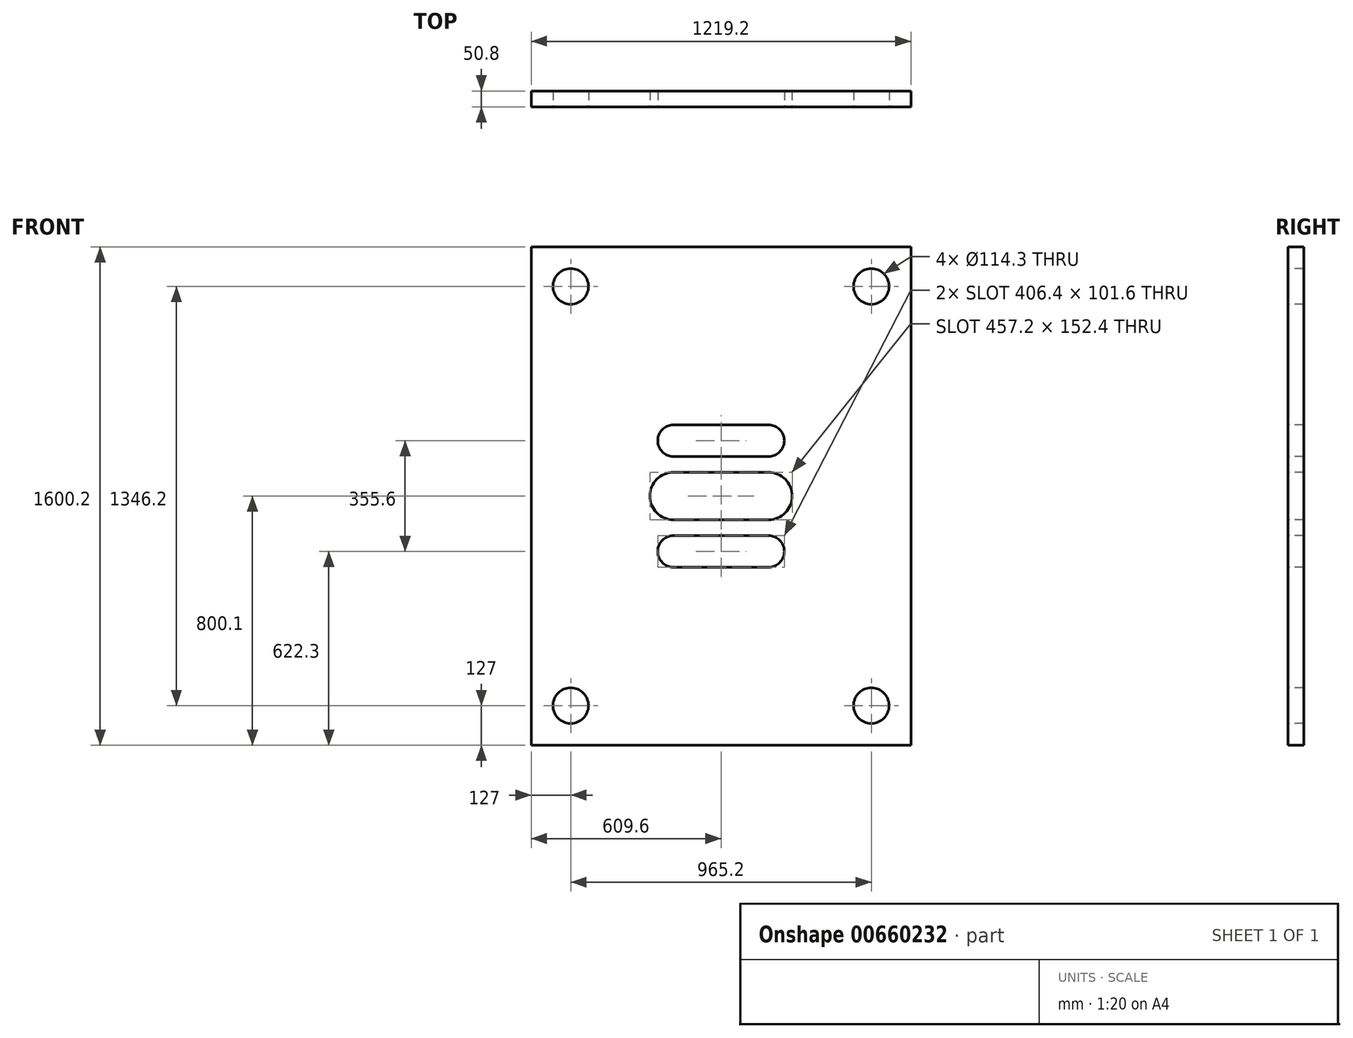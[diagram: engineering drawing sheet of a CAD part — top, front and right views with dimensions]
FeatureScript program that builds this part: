
annotation { "Feature Type Name" : "Feature", "Feature Type Description" : "" }
export const myFeature = defineFeature(function(context is Context, id is Id, definition is map)
    precondition{}
    {
        {
            var Q0;
            Q0=qCreatedBy(makeId("Front.planeOp"),FACE);
            var sketch = newSketch(context, id + "F0", { "sketchPlane" : qUnion([Q0])});
            skLineSegment(sketch, "E0.bottom", {"start": v(-609.6, -800.1) * mm, "end": v(609.6, -800.1) * mm});
            skLineSegment(sketch, "E0.top", {"start": v(-609.6, 800.1) * mm, "end": v(609.6, 800.1) * mm});
            skLineSegment(sketch, "E0.left", {"start": v(-609.6, -800.1) * mm, "end": v(-609.6, 800.1) * mm});
            skLineSegment(sketch, "E0.right", {"start": v(609.6, -800.1) * mm, "end": v(609.6, 800.1) * mm});
            skPoint(sketch, "E0.middle", {"position": v(0, 0) * mm});
            skSolve(sketch);
        }
        {
            var Q0;
            Q0=makeQuery(id+"F0.imprint","IMPRINT",FACE,{"disambiguationData":[TD([[makeQuery(id+"F0.imprint","IMPRINT",EDGE,{"derivedFrom":sQuery(id+"F0.wireOp",EDGE,"E0.bottom")}),1.0]])]});
            var sketch = newSketch(context, id + "F1", { "sketchPlane" : qUnion([Q0])});
            skLineSegment(sketch, "E1", {"start": v(0, 743.78) * mm, "end": v(0, -755.56) * mm, "construction": true});
            skSolve(sketch);
        }
        {
            var Q0;
            Q0=makeQuery(id+"F1.imprint","IMPRINT",FACE,{"disambiguationData":[TD([[makeQuery(id+"F1.imprint","IMPRINT",EDGE,{"derivedFrom":makeQuery(id+"F0.imprint","IMPRINT",EDGE,{"derivedFrom":sQuery(id+"F0.wireOp",EDGE,"E0.bottom")})}),1.0]])]});
            extrude(context, id + "F2", {"entities" : qUnion([Q0]), "depth" : 50.8 * mm, "offsetDistance" : 25.4 * mm});
        }
        {
            var Q0;
            Q0=makeQuery(id+"F2.opExtrude","CAP_FACE",FACE,{"disambiguationData":[OSD([sQuery(id+"F0.wireOp",EDGE,"E0.bottom"),sQuery(id+"F0.wireOp",EDGE,"E0.top"),sQuery(id+"F0.wireOp",EDGE,"E0.left"),sQuery(id+"F0.wireOp",EDGE,"E0.right")])],"isStart":false});
            var sketch = newSketch(context, id + "F3", { "sketchPlane" : qUnion([Q0])});
            skCircle(sketch, "E2", {"center": v(-482.6, 673.1) * mm, "radius": 57.15 * mm});
            skLineSegment(sketch, "E3", {"start": v(-506.12, 0) * mm, "end": v(142.94, 0) * mm, "construction": true});
            skLineSegment(sketch, "E4", {"start": v(0, 664.01) * mm, "end": v(0, -622.38) * mm, "construction": true});
            skCircle(sketch, "E5.MirrorC", {"center": v(482.6, 673.1) * mm, "radius": 57.15 * mm});
            skCircle(sketch, "E6.MirrorC", {"center": v(-482.6, -673.1) * mm, "radius": 57.15 * mm});
            skCircle(sketch, "E7.MirrorC", {"center": v(482.6, -673.1) * mm, "radius": 57.15 * mm});
            skSolve(sketch);
        }
        {
            var Q0;
            Q0 = qSketchRegion(id + "F3", true);
            extrude(context, id + "F4", {"entities" : qUnion([Q0]), "operationType" : NewBodyOperationType.REMOVE, "oppositeDirection" : true, "depth" : 76.2 * mm, "offsetDistance" : 25.4 * mm});
        }
        {
            var Q0;
            Q0=makeQuery(id+"F2.opExtrude","CAP_FACE",FACE,{"disambiguationData":[OSD([sQuery(id+"F0.wireOp",EDGE,"E0.bottom"),sQuery(id+"F0.wireOp",EDGE,"E0.top"),sQuery(id+"F0.wireOp",EDGE,"E0.left"),sQuery(id+"F0.wireOp",EDGE,"E0.right")])],"isStart":false});
            var sketch = newSketch(context, id + "F5", { "sketchPlane" : qUnion([Q0])});
            skLineSegment(sketch, "E8.bottom", {"start": v(-152.4, 127) * mm, "end": v(152.4, 127) * mm});
            skLineSegment(sketch, "E8.top", {"start": v(-152.4, 228.6) * mm, "end": v(152.4, 228.6) * mm});
            skLineSegment(sketch, "E8.left", {"start": v(-152.4, 127) * mm, "end": v(-152.4, 228.6) * mm});
            skLineSegment(sketch, "E8.right", {"start": v(152.4, 127) * mm, "end": v(152.4, 228.6) * mm});
            skPoint(sketch, "E8.middle", {"position": v(0, 177.8) * mm});
            skArc(sketch, "E9", {"start": v(152.4, 127) * mm, "mid": v(203.2, 177.8) * mm, "end": v(152.4, 228.6) * mm});
            skArc(sketch, "E10", {"start": v(-152.4, 228.6) * mm, "mid": v(-203.2, 177.8) * mm, "end": v(-152.4, 127) * mm});
            skLineSegment(sketch, "E11", {"start": v(-215.96, 0) * mm, "end": v(248.62, 0) * mm, "construction": true});
            skLineSegment(sketch, "E12.MirrorCS", {"start": v(-152.4, -127) * mm, "end": v(152.4, -127) * mm});
            skLineSegment(sketch, "E13.MirrorCS", {"start": v(-152.4, -228.6) * mm, "end": v(152.4, -228.6) * mm});
            skArc(sketch, "E14.MirrorCS", {"start": v(152.4, -127) * mm, "mid": v(203.2, -177.8) * mm, "end": v(152.4, -228.6) * mm});
            skArc(sketch, "E15.MirrorCS", {"start": v(-152.4, -228.6) * mm, "mid": v(-203.2, -177.8) * mm, "end": v(-152.4, -127) * mm});
            skLineSegment(sketch, "E16.bottom", {"start": v(-152.4, -76.2) * mm, "end": v(152.4, -76.2) * mm});
            skLineSegment(sketch, "E16.top", {"start": v(-152.4, 76.2) * mm, "end": v(152.4, 76.2) * mm});
            skLineSegment(sketch, "E16.left", {"start": v(-152.4, -76.2) * mm, "end": v(-152.4, 76.2) * mm});
            skLineSegment(sketch, "E16.right", {"start": v(152.4, -76.2) * mm, "end": v(152.4, 76.2) * mm});
            skPoint(sketch, "E16.middle", {"position": v(0, 0) * mm});
            skArc(sketch, "E17", {"start": v(152.4, -76.2) * mm, "mid": v(228.6, 0) * mm, "end": v(152.4, 76.2) * mm});
            skLineSegment(sketch, "E18", {"start": v(0, 0) * mm, "end": v(0, -76.2) * mm, "construction": true});
            skArc(sketch, "E19.MirrorCS", {"start": v(-152.4, -76.2) * mm, "mid": v(-228.6, 0) * mm, "end": v(-152.4, 76.2) * mm});
            skSolve(sketch);
        }
        {
            var Q0;
            Q0 = qSketchRegion(id + "F5", true);
            extrude(context, id + "F6", {"entities" : qUnion([Q0]), "operationType" : NewBodyOperationType.REMOVE, "oppositeDirection" : true, "depth" : 76.2 * mm, "offsetDistance" : 25.4 * mm});
        }
        {
            var Q0;
            Q0 = qSketchRegion(id + "F5", true);
            extrude(context, id + "F7", {"entities" : qUnion([Q0]), "operationType" : NewBodyOperationType.REMOVE, "oppositeDirection" : true, "depth" : 76.2 * mm, "offsetDistance" : 25.4 * mm});
        }
    });
